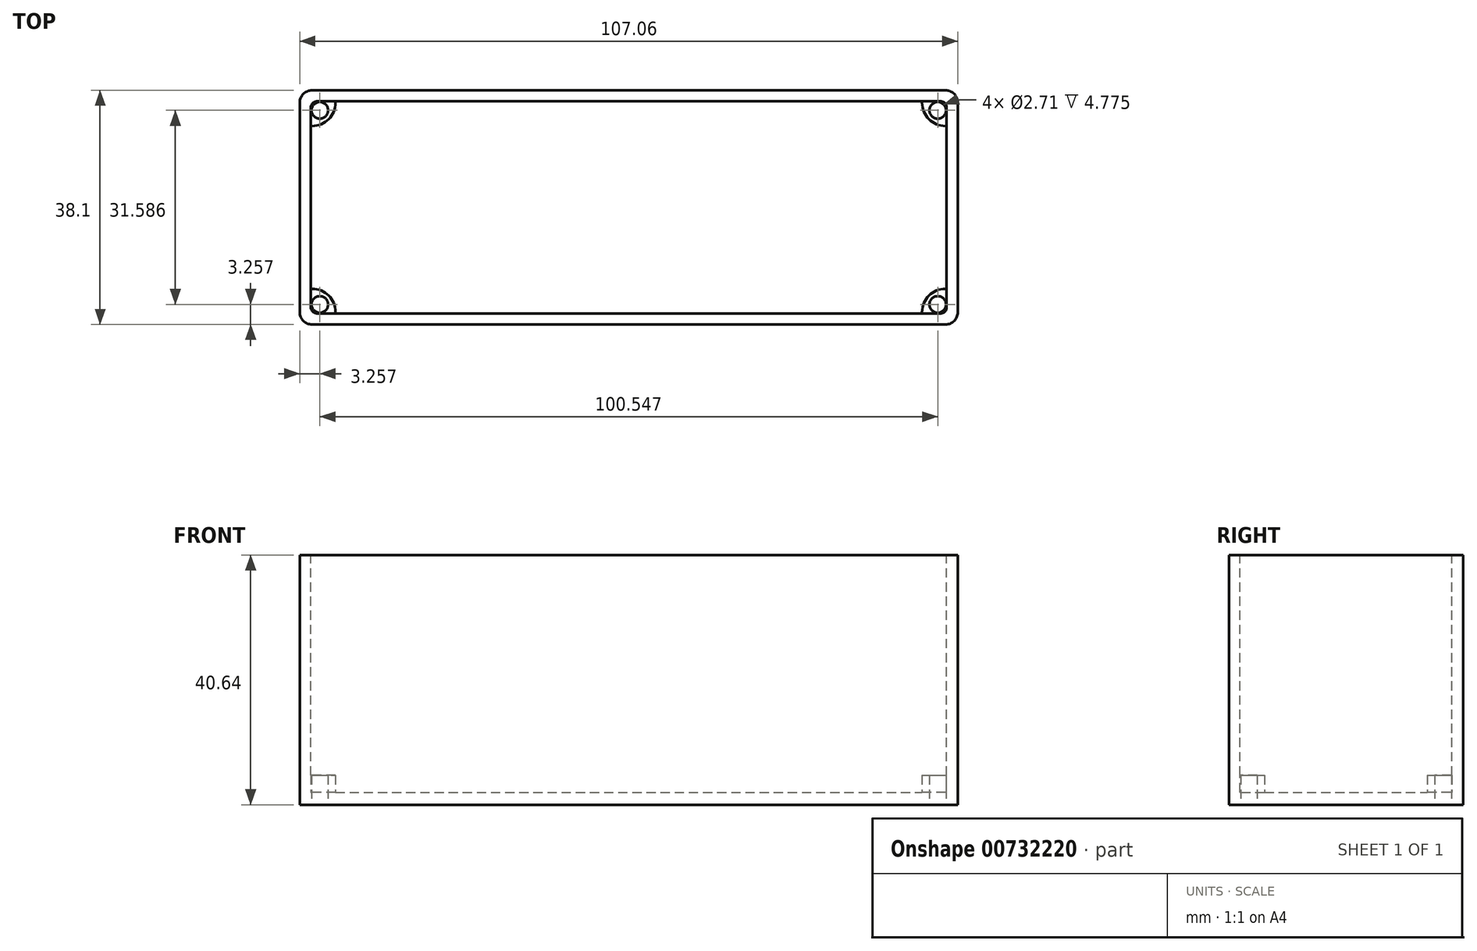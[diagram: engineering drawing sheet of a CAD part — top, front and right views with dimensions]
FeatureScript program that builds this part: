
annotation { "Feature Type Name" : "Feature", "Feature Type Description" : "" }
export const myFeature = defineFeature(function(context is Context, id is Id, definition is map)
    precondition{}
    {
        {
            var Q0;
            Q0=qCreatedBy(makeId("Top.planeOp"),FACE);
            var sketch = newSketch(context, id + "F0", { "sketchPlane" : qUnion([Q0])});
            skLineSegment(sketch, "E0.bottom", {"start": v(2, 0) * mm, "end": v(105.06, 0) * mm});
            skLineSegment(sketch, "E0.top", {"start": v(2, 38.1) * mm, "end": v(105.06, 38.1) * mm});
            skLineSegment(sketch, "E0.left", {"start": v(0, 2) * mm, "end": v(0, 36.1) * mm});
            skLineSegment(sketch, "E0.right", {"start": v(107.06, 2) * mm, "end": v(107.06, 36.1) * mm});
            skPoint(sketch, "E1.visualSharp", {"position": v(0, 38.1) * mm});
            skArc(sketch, "E1.filletArc", {"start": v(2, 38.1) * mm, "mid": v(0.59, 37.51) * mm, "end": v(0, 36.1) * mm});
            skPoint(sketch, "E2.visualSharp", {"position": v(107.06, 38.1) * mm});
            skArc(sketch, "E2.filletArc", {"start": v(107.06, 36.1) * mm, "mid": v(106.48, 37.51) * mm, "end": v(105.06, 38.1) * mm});
            skPoint(sketch, "E3.visualSharp", {"position": v(107.06, 0) * mm});
            skArc(sketch, "E3.filletArc", {"start": v(105.06, 0) * mm, "mid": v(106.48, 0.59) * mm, "end": v(107.06, 2) * mm});
            skPoint(sketch, "E4.visualSharp", {"position": v(0, 0) * mm});
            skArc(sketch, "E4.filletArc", {"start": v(0, 2) * mm, "mid": v(0.59, 0.59) * mm, "end": v(2, 0) * mm});
            skSolve(sketch);
        }
        {
            var Q0;
            Q0=qSketchRegion(id+"F0",true);
            var Q1;
            Q1=qSketchRegion(id+"F2",true);
            extrude(context, id + "F1", {"entities" : qUnion([Q0, Q1]), "depth" : 40.64 * mm, "offsetDistance" : 25 * mm});
        }
        {
            var Q0;
            Q0=makeQuery(id+"F1.opExtrude","CAP_FACE",FACE,{"disambiguationData":[OSD([sQuery(id+"F0.wireOp",EDGE,"E0.bottom"),sQuery(id+"F0.wireOp",EDGE,"E0.top"),sQuery(id+"F0.wireOp",EDGE,"E0.left"),sQuery(id+"F0.wireOp",EDGE,"E0.right"),sQuery(id+"F0.wireOp",EDGE,"E1.filletArc"),sQuery(id+"F0.wireOp",EDGE,"E2.filletArc"),sQuery(id+"F0.wireOp",EDGE,"E3.filletArc"),sQuery(id+"F0.wireOp",EDGE,"E4.filletArc")])],"isStart":false});
            var sketch = newSketch(context, id + "F2", { "sketchPlane" : qUnion([Q0])});
            skLineSegment(sketch, "E5.0", {"start": v(2, 38.1) * mm, "end": v(105.06, 38.1) * mm});
            skLineSegment(sketch, "E6.0", {"start": v(0, 2) * mm, "end": v(0, 36.1) * mm});
            skLineSegment(sketch, "E7.0", {"start": v(107.06, 2) * mm, "end": v(107.06, 36.1) * mm});
            skLineSegment(sketch, "E8.0", {"start": v(2, 0) * mm, "end": v(105.06, 0) * mm});
            skArc(sketch, "E9.0", {"start": v(2, 38.1) * mm, "mid": v(0.59, 37.51) * mm, "end": v(0, 36.1) * mm});
            skArc(sketch, "E10.0", {"start": v(107.06, 36.1) * mm, "mid": v(106.48, 37.51) * mm, "end": v(105.06, 38.1) * mm});
            skLineSegment(sketch, "E11.0", {"start": v(2.8, 36.3) * mm, "end": v(104.26, 36.3) * mm});
            skLineSegment(sketch, "E11.1", {"start": v(1.8, 2.8) * mm, "end": v(1.8, 35.3) * mm});
            skLineSegment(sketch, "E11.2", {"start": v(2.8, 1.8) * mm, "end": v(104.26, 1.8) * mm});
            skLineSegment(sketch, "E11.3", {"start": v(105.26, 2.8) * mm, "end": v(105.26, 35.3) * mm});
            skPoint(sketch, "E12.visualSharp", {"position": v(1.8, 36.3) * mm});
            skArc(sketch, "E12.filletArc", {"start": v(2.8, 36.3) * mm, "mid": v(2.1, 36) * mm, "end": v(1.8, 35.3) * mm});
            skPoint(sketch, "E13.visualSharp", {"position": v(1.8, 1.8) * mm});
            skArc(sketch, "E13.filletArc", {"start": v(1.8, 2.8) * mm, "mid": v(2.1, 2.1) * mm, "end": v(2.8, 1.8) * mm});
            skPoint(sketch, "E14.visualSharp", {"position": v(105.26, 1.8) * mm});
            skArc(sketch, "E14.filletArc", {"start": v(104.26, 1.8) * mm, "mid": v(104.97, 2.1) * mm, "end": v(105.26, 2.8) * mm});
            skPoint(sketch, "E15.visualSharp", {"position": v(105.26, 36.3) * mm});
            skArc(sketch, "E15.filletArc", {"start": v(105.26, 35.3) * mm, "mid": v(104.97, 36) * mm, "end": v(104.26, 36.3) * mm});
            skSolve(sketch);
        }
        {
            var Q0;
            Q0=qSketchRegion(id+"F2",true);
            extrude(context, id + "F3", {"entities" : qUnion([Q0]), "operationType" : NewBodyOperationType.REMOVE, "oppositeDirection" : true, "depth" : 38.6 * mm, "offsetDistance" : 25.4 * mm});
        }
        {
            var Q0;
            Q0=makeQuery(id+"F1.opExtrude","CAP_FACE",FACE,{"disambiguationData":[OSD([sQuery(id+"F0.wireOp",EDGE,"E0.bottom"),sQuery(id+"F0.wireOp",EDGE,"E0.top"),sQuery(id+"F0.wireOp",EDGE,"E0.left"),sQuery(id+"F0.wireOp",EDGE,"E0.right"),sQuery(id+"F0.wireOp",EDGE,"E1.filletArc"),sQuery(id+"F0.wireOp",EDGE,"E2.filletArc"),sQuery(id+"F0.wireOp",EDGE,"E3.filletArc"),sQuery(id+"F0.wireOp",EDGE,"E4.filletArc")])],"isStart":true});
            var sketch = newSketch(context, id + "F4", { "sketchPlane" : qUnion([Q0])});
            skArc(sketch, "E16.0", {"start": v(105.06, 0) * mm, "mid": v(106.48, -0.59) * mm, "end": v(107.06, -2) * mm});
            skArc(sketch, "E17", {"start": v(105.06, -5.8) * mm, "mid": v(102.37, -4.7) * mm, "end": v(101.25, -2) * mm});
            skLineSegment(sketch, "E18", {"start": v(105.06, -5.81) * mm, "end": v(107.06, -5.81) * mm});
            skLineSegment(sketch, "E19", {"start": v(107.06, -5.81) * mm, "end": v(107.06, -2) * mm});
            skLineSegment(sketch, "E20", {"start": v(101.25, -2) * mm, "end": v(101.25, 0) * mm});
            skLineSegment(sketch, "E21", {"start": v(101.25, 0) * mm, "end": v(105.06, 0) * mm});
            skLineSegment(sketch, "E22", {"start": v(53.53, -38.1) * mm, "end": v(53.53, 0) * mm, "construction": true});
            skLineSegment(sketch, "E23", {"start": v(107.06, -19.05) * mm, "end": v(0, -19.05) * mm, "construction": true});
            skLineSegment(sketch, "E24.MirrorCS", {"start": v(101.25, -38.1) * mm, "end": v(105.06, -38.1) * mm});
            skLineSegment(sketch, "E25.MirrorCS", {"start": v(101.25, -36.1) * mm, "end": v(101.25, -38.1) * mm});
            skLineSegment(sketch, "E26.MirrorCS", {"start": v(105.06, -32.3) * mm, "end": v(107.06, -32.3) * mm});
            skLineSegment(sketch, "E27.MirrorCS", {"start": v(107.06, -32.29) * mm, "end": v(107.06, -36.1) * mm});
            skArc(sketch, "E28.MirrorCS", {"start": v(105.06, -32.3) * mm, "mid": v(102.37, -33.4) * mm, "end": v(101.25, -36.1) * mm});
            skArc(sketch, "E29.MirrorCS", {"start": v(105.06, -38.1) * mm, "mid": v(106.48, -37.51) * mm, "end": v(107.06, -36.1) * mm});
            skArc(sketch, "E30.MirrorCS", {"start": v(2, -32.3) * mm, "mid": v(4.7, -33.4) * mm, "end": v(5.8, -36.1) * mm});
            skLineSegment(sketch, "E31.MirrorCS", {"start": v(0, -32.3) * mm, "end": v(0, -36.1) * mm});
            skLineSegment(sketch, "E32.MirrorCS", {"start": v(2, -32.3) * mm, "end": v(0, -32.3) * mm});
            skLineSegment(sketch, "E33.MirrorCS", {"start": v(5.81, -36.1) * mm, "end": v(5.81, -38.1) * mm});
            skLineSegment(sketch, "E34.MirrorCS", {"start": v(5.81, -38.1) * mm, "end": v(2, -38.1) * mm});
            skArc(sketch, "E35.MirrorCS", {"start": v(2, -38.1) * mm, "mid": v(0.59, -37.51) * mm, "end": v(0, -36.1) * mm});
            skArc(sketch, "E36.MirrorCS", {"start": v(2, 0) * mm, "mid": v(0.59, -0.59) * mm, "end": v(0, -2) * mm});
            skArc(sketch, "E37.MirrorCS", {"start": v(2, -5.8) * mm, "mid": v(4.7, -4.7) * mm, "end": v(5.8, -2) * mm});
            skLineSegment(sketch, "E38.MirrorCS", {"start": v(2, -5.81) * mm, "end": v(0, -5.81) * mm});
            skLineSegment(sketch, "E39.MirrorCS", {"start": v(0, -5.81) * mm, "end": v(0, -2) * mm});
            skLineSegment(sketch, "E40.MirrorCS", {"start": v(5.81, 0) * mm, "end": v(2, 0) * mm});
            skLineSegment(sketch, "E41.MirrorCS", {"start": v(5.8, -2) * mm, "end": v(5.8, 0) * mm});
            skSolve(sketch);
        }
        {
            var Q0;
            Q0 = qSketchRegion(id + "F4", true);
            extrude(context, id + "F5", {"entities" : qUnion([Q0]), "operationType" : NewBodyOperationType.ADD, "oppositeDirection" : true, "depth" : 4.78 * mm, "offsetDistance" : 25.4 * mm});
        }
        {
            var Q0;
            Q0=makeQuery(id+"F1.opExtrude","CAP_FACE",FACE,{"disambiguationData":[OSD([sQuery(id+"F0.wireOp",EDGE,"E0.bottom"),sQuery(id+"F0.wireOp",EDGE,"E0.top"),sQuery(id+"F0.wireOp",EDGE,"E0.left"),sQuery(id+"F0.wireOp",EDGE,"E0.right"),sQuery(id+"F0.wireOp",EDGE,"E1.filletArc"),sQuery(id+"F0.wireOp",EDGE,"E2.filletArc"),sQuery(id+"F0.wireOp",EDGE,"E3.filletArc"),sQuery(id+"F0.wireOp",EDGE,"E4.filletArc")])],"isStart":true});
            var sketch = newSketch(context, id + "F6", { "sketchPlane" : qUnion([Q0])});
            skCircle(sketch, "E42", {"center": v(103.8, -3.26) * mm, "radius": 1.35 * mm});
            skLineSegment(sketch, "E43", {"start": v(106.48, -0.59) * mm, "end": v(102.37, -4.7) * mm, "construction": true});
            skCircle(sketch, "E44.MirrorC", {"center": v(3.26, -3.26) * mm, "radius": 1.35 * mm});
            skCircle(sketch, "E45.MirrorC", {"center": v(3.26, -34.84) * mm, "radius": 1.35 * mm});
            skCircle(sketch, "E46.MirrorC", {"center": v(103.8, -34.84) * mm, "radius": 1.35 * mm});
            skSolve(sketch);
        }
        {
            var Q0;
            Q0 = qSketchRegion(id + "F6", true);
            extrude(context, id + "F7", {"entities" : qUnion([Q0]), "operationType" : NewBodyOperationType.REMOVE, "endBound" : BoundingType.UP_TO_NEXT, "oppositeDirection" : true, "depth" : 5.08 * mm, "offsetDistance" : 25.4 * mm});
        }
    });
